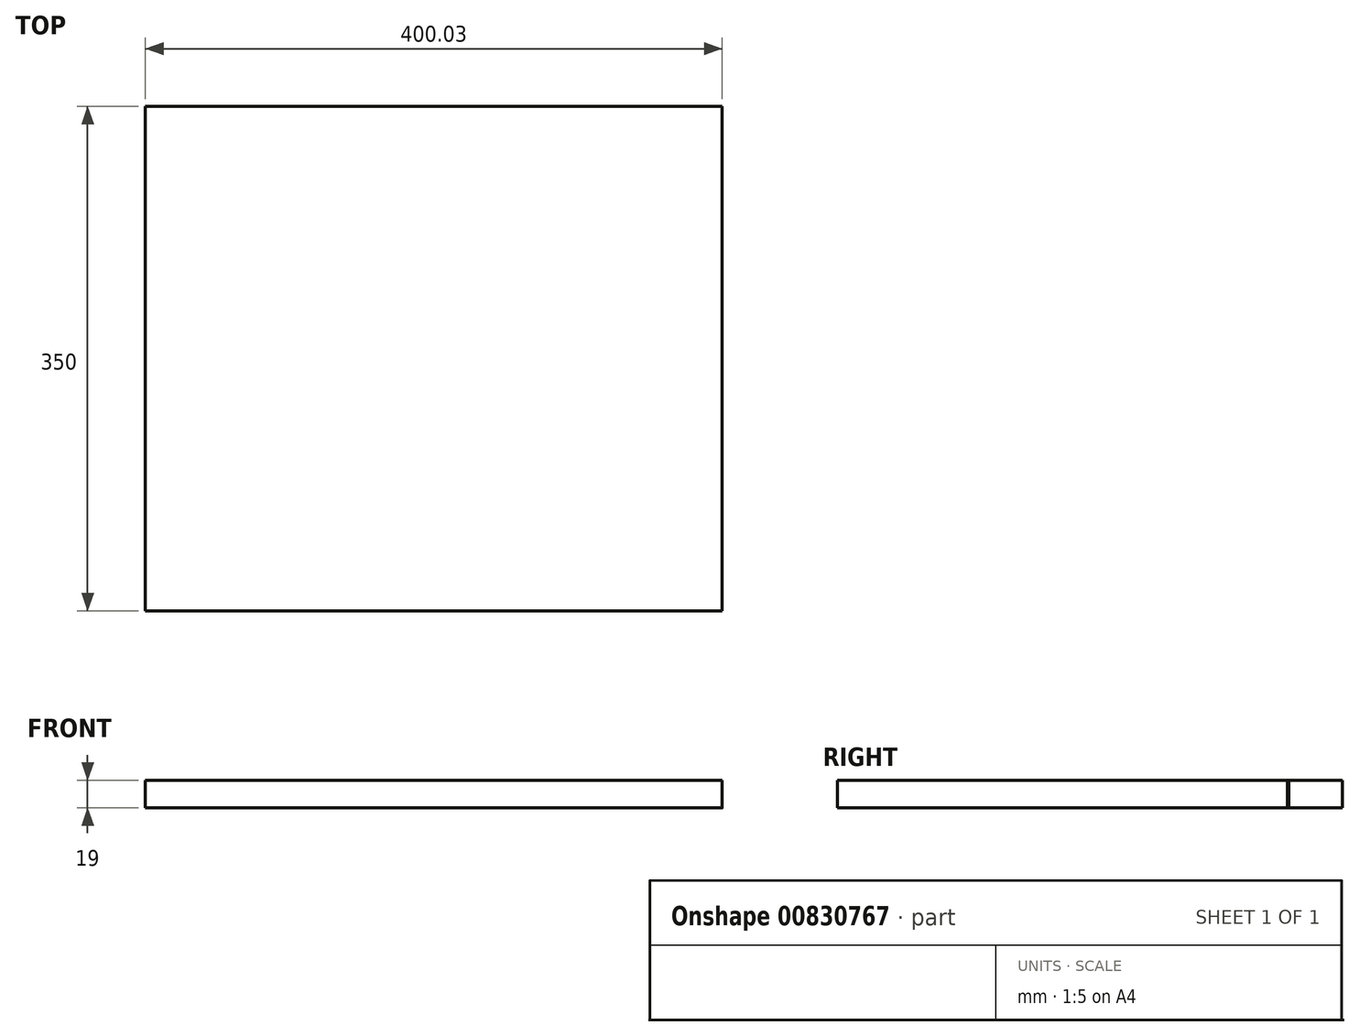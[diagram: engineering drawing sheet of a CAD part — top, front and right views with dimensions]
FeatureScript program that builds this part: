
annotation { "Feature Type Name" : "Feature", "Feature Type Description" : "" }
export const myFeature = defineFeature(function(context is Context, id is Id, definition is map)
    precondition{}
    {
        {
            var Q0;
            Q0=qCreatedBy(makeId("Top.planeOp"),FACE);
            var sketch = newSketch(context, id + "F0", { "sketchPlane" : qUnion([Q0])});
            skLineSegment(sketch, "E0.bottom", {"start": v(200, 162.85) * mm, "end": v(-200, 162.85) * mm});
            skLineSegment(sketch, "E0.top", {"start": v(200, -187.15) * mm, "end": v(-200, -187.15) * mm});
            skLineSegment(sketch, "E0.left", {"start": v(200, 162.85) * mm, "end": v(200, -187.15) * mm});
            skLineSegment(sketch, "E0.right", {"start": v(-200, 162.85) * mm, "end": v(-200, -187.15) * mm});
            skPoint(sketch, "E0.middle", {"position": v(0, -12.15) * mm});
            skFitSpline(sketch, "E1", {"points": [v(-200, -132.62) * mm, v(-186.96, -170.24) * mm, v(-133.02, -187.15) * mm], "startDerivative": vector(0, -145.86) * mm, "endDerivative": vector(193.13, 0) * mm});
            skFitSpline(sketch, "E2", {"points": [v(-200, 104.91) * mm, v(-184.65, 149.42) * mm, v(-153.68, 162.85) * mm], "startDerivative": vector(0, 148.63) * mm, "endDerivative": vector(117.15, 0) * mm});
            skFitSpline(sketch, "E3", {"points": [v(159.78, 162.85) * mm, v(189.76, 149.42) * mm, v(200, 125.76) * mm, v(200, 125) * mm], "startDerivative": vector(56.88, -15.68) * mm, "endDerivative": vector(-1.38, -5.92) * mm});
            skFitSpline(sketch, "E4", {"points": [v(200, -133.33) * mm, v(187.45, -171.77) * mm, v(157.47, -187.15) * mm], "startDerivative": vector(-17.95, -71.86) * mm, "endDerivative": vector(-55.78, -21.6) * mm});
            skSolve(sketch);
        }
        {
            var Q0;
            {var subQ3=sQuery(id+"F0.wireOp",EDGE,"E1");Q0=makeQuery(id+"F0.imprint","IMPRINT",FACE,{"disambiguationData":[TD([[makeQuery(id+"F0.imprint","IMPRINT",EDGE,{"derivedFrom":subQ3}),-1.0]])]});}
            var Q1;
            {var subQ3=sQuery(id+"F0.wireOp",EDGE,"E4");Q1=makeQuery(id+"F0.imprint","IMPRINT",FACE,{"disambiguationData":[TD([[makeQuery(id+"F0.imprint","IMPRINT",EDGE,{"derivedFrom":subQ3}),1.0]])]});}
            var Q2;
            {var subQ0=sQuery(id+"F0.wireOp",EDGE,"E3");var subQ1=sQuery(id+"F0.wireOp",EDGE,"E0.left");var subQ2=makeQuery(id+"F0.imprint","INTERSECT",VERTEX,{"disambiguationData":[OD(0.0)],"derivedFrom":[subQ1,subQ0]});Q2=makeQuery(id+"F0.imprint","IMPRINT",FACE,{"disambiguationData":[TD([[makeQuery(id+"F0.imprint","IMPRINT",EDGE,{"disambiguationData":[TD([[subQ2,1.0]])],"derivedFrom":subQ1}),1.0]])]});}
            var Q3;
            {var subQ5=sQuery(id+"F0.wireOp",EDGE,"E1");Q3=makeQuery(id+"F0.imprint","IMPRINT",FACE,{"disambiguationData":[TD([[makeQuery(id+"F0.imprint","IMPRINT",EDGE,{"derivedFrom":subQ5}),1.0]])]});}
            var Q4;
            {var subQ3=sQuery(id+"F0.wireOp",EDGE,"E2");Q4=makeQuery(id+"F0.imprint","IMPRINT",FACE,{"disambiguationData":[TD([[makeQuery(id+"F0.imprint","IMPRINT",EDGE,{"derivedFrom":subQ3}),1.0]])]});}
            var Q5;
            {var subQ0=sQuery(id+"F0.wireOp",EDGE,"E0.left");var subQ1=sQuery(id+"F0.wireOp",EDGE,"E0.bottom");var subQ2=makeQuery(id+"F0.imprint","INTERSECT",VERTEX,{"derivedFrom":[subQ1,subQ0]});Q5=makeQuery(id+"F0.imprint","IMPRINT",FACE,{"disambiguationData":[TD([[makeQuery(id+"F0.imprint","IMPRINT",EDGE,{"disambiguationData":[TD([[subQ2,-1.0]])],"derivedFrom":subQ1}),1.0]])]});}
            extrude(context, id + "F1", {"entities" : qUnion([Q0, Q1, Q2, Q3, Q4, Q5]), "depth" : 19 * mm, "offsetDistance" : 25 * mm});
        }
        {
            var Q0;
            {var subQ3=sQuery(id+"F0.wireOp",EDGE,"E1");Q0=makeQuery(id+"F0.imprint","IMPRINT",FACE,{"disambiguationData":[TD([[makeQuery(id+"F0.imprint","IMPRINT",EDGE,{"derivedFrom":subQ3}),-1.0]])]});}
            extrude(context, id + "F2", {"entities" : qUnion([Q0]), "operationType" : NewBodyOperationType.REMOVE, "endBound" : BoundingType.THROUGH_ALL, "oppositeDirection" : true, "depth" : 25 * mm, "offsetDistance" : 25 * mm});
        }
        {
            var Q0;
            {var subQ3=sQuery(id+"F0.wireOp",EDGE,"E2");Q0=makeQuery(id+"F0.imprint","IMPRINT",FACE,{"disambiguationData":[TD([[makeQuery(id+"F0.imprint","IMPRINT",EDGE,{"derivedFrom":subQ3}),1.0]])]});}
            extrude(context, id + "F3", {"entities" : qUnion([Q0]), "operationType" : NewBodyOperationType.REMOVE, "endBound" : BoundingType.THROUGH_ALL, "oppositeDirection" : true, "depth" : 25 * mm, "offsetDistance" : 25 * mm});
        }
    });
